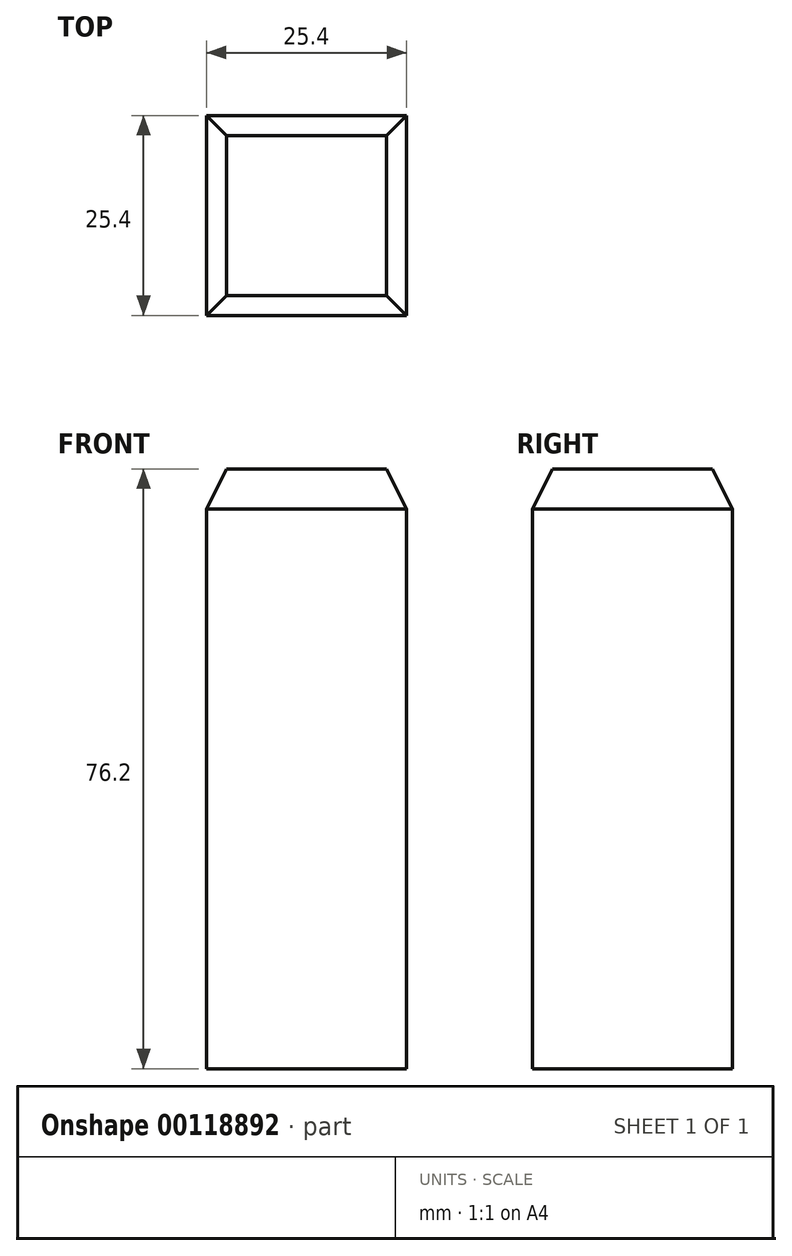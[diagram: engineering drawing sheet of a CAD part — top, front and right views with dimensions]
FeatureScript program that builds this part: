
annotation { "Feature Type Name" : "Feature", "Feature Type Description" : "" }
export const myFeature = defineFeature(function(context is Context, id is Id, definition is map)
    precondition{}
    {
        {
            var Q0;
            Q0=qCreatedBy(makeId("Top.planeOp"),FACE);
            var sketch = newSketch(context, id + "F0", { "sketchPlane" : qUnion([Q0])});
            skLineSegment(sketch, "E0.bottom", {"start": v(3.6, 0) * mm, "end": v(29, 0) * mm});
            skLineSegment(sketch, "E0.top", {"start": v(3.6, 25.4) * mm, "end": v(29, 25.4) * mm});
            skLineSegment(sketch, "E0.left", {"start": v(3.6, 0) * mm, "end": v(3.6, 25.4) * mm});
            skLineSegment(sketch, "E0.right", {"start": v(29, 0) * mm, "end": v(29, 25.4) * mm});
            skLineSegment(sketch, "E1.bottom", {"start": v(38.96, 81.11) * mm, "end": v(39.68, 81.11) * mm});
            skLineSegment(sketch, "E1.top", {"start": v(38.96, 74.35) * mm, "end": v(39.68, 74.35) * mm});
            skLineSegment(sketch, "E1.left", {"start": v(38.96, 81.11) * mm, "end": v(38.96, 74.35) * mm});
            skLineSegment(sketch, "E1.right", {"start": v(39.68, 81.11) * mm, "end": v(39.68, 74.35) * mm});
            skSolve(sketch);
        }
        {
            var Q0;
            Q0=makeQuery(id+"F0.imprint","IMPRINT",FACE,{"disambiguationData":[TD([[makeQuery(id+"F0.imprint","IMPRINT",EDGE,{"derivedFrom":sQuery(id+"F0.wireOp",EDGE,"E0.bottom")}),1.0]])]});
            extrude(context, id + "F1", {"entities" : qUnion([Q0]), "depth" : 76.2 * mm});
        }
        {
            var Q0;
            Q0=makeQuery(id+"F1.opExtrude","CAP_EDGE",EDGE,{"disambiguationData":[OSD([sQuery(id+"F0.wireOp",EDGE,"E0.right")])],"isStart":false});
            var Q1;
            Q1=makeQuery(id+"F1.opExtrude","CAP_EDGE",EDGE,{"disambiguationData":[OSD([sQuery(id+"F0.wireOp",EDGE,"E0.bottom")])],"isStart":false});
            var Q2;
            Q2=makeQuery(id+"F1.opExtrude","CAP_EDGE",EDGE,{"disambiguationData":[OSD([sQuery(id+"F0.wireOp",EDGE,"E0.left")])],"isStart":false});
            var Q3;
            Q3=makeQuery(id+"F1.opExtrude","CAP_EDGE",EDGE,{"disambiguationData":[OSD([sQuery(id+"F0.wireOp",EDGE,"E0.top")])],"isStart":false});
            chamfer(context, id + "F2", {"entities" : qUnion([Q0, Q1, Q2, Q3]), "chamferType" : ChamferType.TWO_OFFSETS, "width1" : 2.54 * mm, "oppositeDirection" : false, "width2" : 5.08 * mm, "tangentPropagation" : true});
        }
    });
